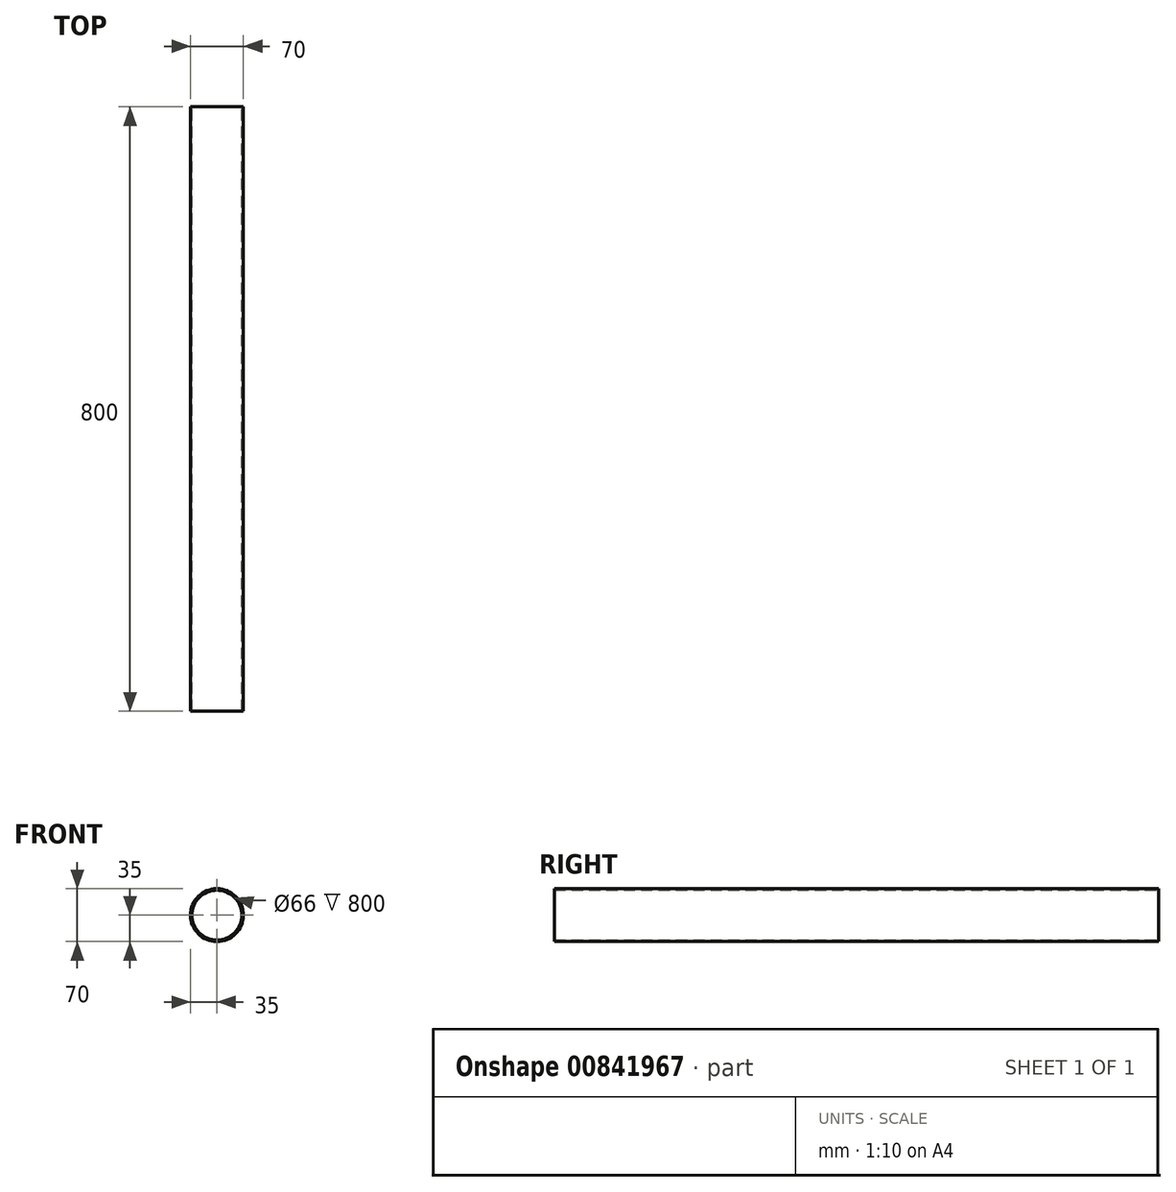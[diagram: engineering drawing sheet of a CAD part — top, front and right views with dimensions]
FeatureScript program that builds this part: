
annotation { "Feature Type Name" : "Feature", "Feature Type Description" : "" }
export const myFeature = defineFeature(function(context is Context, id is Id, definition is map)
    precondition{}
    {
        {
            var Q0;
            Q0=qCreatedBy(makeId("Front.planeOp"),FACE);
            var sketch = newSketch(context, id + "F0", { "sketchPlane" : qUnion([Q0])});
            skCircle(sketch, "E0", {"center": v(0, 0) * mm, "radius": 35 * mm});
            skCircle(sketch, "E1.0", {"center": v(0, 0) * mm, "radius": 33 * mm});
            skSolve(sketch);
        }
        {
            var Q0;
            Q0=makeQuery(id+"F0.imprint","IMPRINT",FACE,{"disambiguationData":[TD([[makeQuery(id+"F0.imprint","IMPRINT",EDGE,{"derivedFrom":sQuery(id+"F0.wireOp",EDGE,"E0")}),1.0]])]});
            extrude(context, id + "F1", {"entities" : qUnion([Q0]), "endBound" : BoundingType.SYMMETRIC, "depth" : 800 * mm, "offsetDistance" : 25 * mm});
        }
    });
